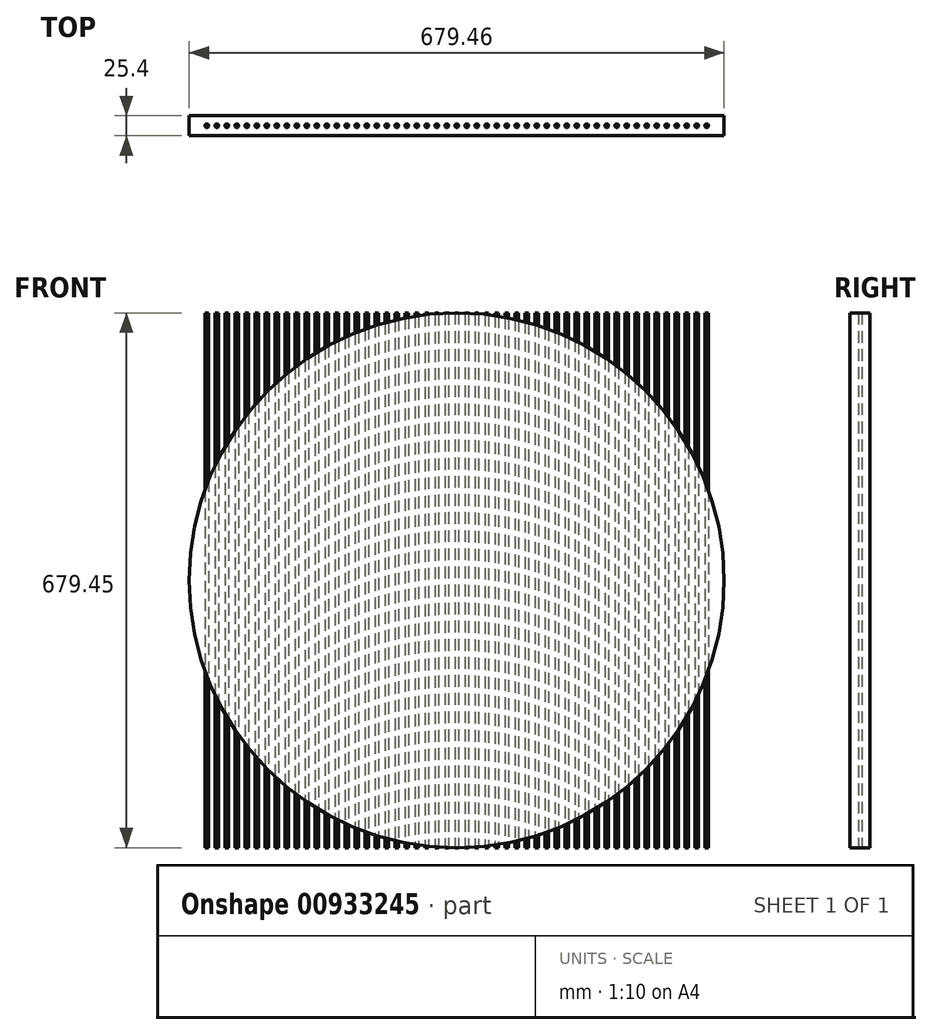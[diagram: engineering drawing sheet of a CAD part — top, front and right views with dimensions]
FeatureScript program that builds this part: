
annotation { "Feature Type Name" : "Feature", "Feature Type Description" : "" }
export const myFeature = defineFeature(function(context is Context, id is Id, definition is map)
    precondition{}
    {
        {
            var Q0;
            Q0=qCreatedBy(makeId("Top.planeOp"),FACE);
            var sketch = newSketch(context, id + "F0", { "sketchPlane" : qUnion([Q0])});
            skCircle(sketch, "E0", {"center": v(0, 0) * mm, "radius": 2.39 * mm});
            skCircle(sketch, "E1.1.0.0", {"center": v(12.7, 0) * mm, "radius": 2.39 * mm});
            skCircle(sketch, "E1.2.0.0", {"center": v(25.4, 0) * mm, "radius": 2.39 * mm});
            skCircle(sketch, "E1.3.0.0", {"center": v(38.1, 0) * mm, "radius": 2.39 * mm});
            skCircle(sketch, "E1.4.0.0", {"center": v(50.8, 0) * mm, "radius": 2.39 * mm});
            skCircle(sketch, "E1.5.0.0", {"center": v(63.5, 0) * mm, "radius": 2.39 * mm});
            skCircle(sketch, "E1.6.0.0", {"center": v(76.2, 0) * mm, "radius": 2.39 * mm});
            skCircle(sketch, "E1.7.0.0", {"center": v(88.9, 0) * mm, "radius": 2.39 * mm});
            skCircle(sketch, "E1.8.0.0", {"center": v(101.6, 0) * mm, "radius": 2.39 * mm});
            skCircle(sketch, "E1.9.0.0", {"center": v(114.3, 0) * mm, "radius": 2.39 * mm});
            skCircle(sketch, "E1.10.0.0", {"center": v(127, 0) * mm, "radius": 2.39 * mm});
            skCircle(sketch, "E1.11.0.0", {"center": v(139.7, 0) * mm, "radius": 2.39 * mm});
            skCircle(sketch, "E1.12.0.0", {"center": v(152.4, 0) * mm, "radius": 2.39 * mm});
            skCircle(sketch, "E1.13.0.0", {"center": v(165.1, 0) * mm, "radius": 2.39 * mm});
            skCircle(sketch, "E1.14.0.0", {"center": v(177.8, 0) * mm, "radius": 2.39 * mm});
            skCircle(sketch, "E1.15.0.0", {"center": v(190.5, 0) * mm, "radius": 2.39 * mm});
            skCircle(sketch, "E1.16.0.0", {"center": v(203.2, 0) * mm, "radius": 2.39 * mm});
            skCircle(sketch, "E1.17.0.0", {"center": v(215.9, 0) * mm, "radius": 2.39 * mm});
            skCircle(sketch, "E1.18.0.0", {"center": v(228.6, 0) * mm, "radius": 2.39 * mm});
            skCircle(sketch, "E1.19.0.0", {"center": v(241.3, 0) * mm, "radius": 2.39 * mm});
            skCircle(sketch, "E1.20.0.0", {"center": v(254, 0) * mm, "radius": 2.39 * mm});
            skCircle(sketch, "E1.21.0.0", {"center": v(266.7, 0) * mm, "radius": 2.39 * mm});
            skCircle(sketch, "E1.22.0.0", {"center": v(279.4, 0) * mm, "radius": 2.39 * mm});
            skCircle(sketch, "E1.23.0.0", {"center": v(292.1, 0) * mm, "radius": 2.39 * mm});
            skCircle(sketch, "E1.24.0.0", {"center": v(304.8, 0) * mm, "radius": 2.39 * mm});
            skCircle(sketch, "E1.25.0.0", {"center": v(317.5, 0) * mm, "radius": 2.39 * mm});
            skLineSegment(sketch, "E1.direction1", {"start": v(0, 0) * mm, "end": v(12.7, 0) * mm, "construction": true});
            skCircle(sketch, "E2.1.0.0", {"center": v(-12.7, 0) * mm, "radius": 2.39 * mm});
            skCircle(sketch, "E2.2.0.0", {"center": v(-25.4, 0) * mm, "radius": 2.39 * mm});
            skCircle(sketch, "E2.3.0.0", {"center": v(-38.1, 0) * mm, "radius": 2.39 * mm});
            skCircle(sketch, "E2.4.0.0", {"center": v(-50.8, 0) * mm, "radius": 2.39 * mm});
            skCircle(sketch, "E2.5.0.0", {"center": v(-63.5, 0) * mm, "radius": 2.39 * mm});
            skCircle(sketch, "E2.6.0.0", {"center": v(-76.2, 0) * mm, "radius": 2.39 * mm});
            skCircle(sketch, "E2.7.0.0", {"center": v(-88.9, 0) * mm, "radius": 2.39 * mm});
            skCircle(sketch, "E2.8.0.0", {"center": v(-101.6, 0) * mm, "radius": 2.39 * mm});
            skCircle(sketch, "E2.9.0.0", {"center": v(-114.3, 0) * mm, "radius": 2.39 * mm});
            skCircle(sketch, "E2.10.0.0", {"center": v(-127, 0) * mm, "radius": 2.39 * mm});
            skCircle(sketch, "E2.11.0.0", {"center": v(-139.7, 0) * mm, "radius": 2.39 * mm});
            skCircle(sketch, "E2.12.0.0", {"center": v(-152.4, 0) * mm, "radius": 2.39 * mm});
            skCircle(sketch, "E2.13.0.0", {"center": v(-165.1, 0) * mm, "radius": 2.39 * mm});
            skCircle(sketch, "E2.14.0.0", {"center": v(-177.8, 0) * mm, "radius": 2.39 * mm});
            skCircle(sketch, "E2.15.0.0", {"center": v(-190.5, 0) * mm, "radius": 2.39 * mm});
            skCircle(sketch, "E2.16.0.0", {"center": v(-203.2, 0) * mm, "radius": 2.39 * mm});
            skCircle(sketch, "E2.17.0.0", {"center": v(-215.9, 0) * mm, "radius": 2.39 * mm});
            skCircle(sketch, "E2.18.0.0", {"center": v(-228.6, 0) * mm, "radius": 2.39 * mm});
            skCircle(sketch, "E2.19.0.0", {"center": v(-241.3, 0) * mm, "radius": 2.39 * mm});
            skCircle(sketch, "E2.20.0.0", {"center": v(-254, 0) * mm, "radius": 2.39 * mm});
            skCircle(sketch, "E2.21.0.0", {"center": v(-266.7, 0) * mm, "radius": 2.39 * mm});
            skCircle(sketch, "E2.22.0.0", {"center": v(-279.4, 0) * mm, "radius": 2.39 * mm});
            skCircle(sketch, "E2.23.0.0", {"center": v(-292.1, 0) * mm, "radius": 2.39 * mm});
            skCircle(sketch, "E2.24.0.0", {"center": v(-304.8, 0) * mm, "radius": 2.39 * mm});
            skCircle(sketch, "E2.25.0.0", {"center": v(-317.5, 0) * mm, "radius": 2.39 * mm});
            skLineSegment(sketch, "E2.direction1", {"start": v(0, 0) * mm, "end": v(-12.7, 0) * mm, "construction": true});
            skSolve(sketch);
        }
        {
            var Q0;
            Q0 = qSketchRegion(id + "F0", true);
            extrude(context, id + "F1", {"entities" : qUnion([Q0]), "depth" : 679.45 * mm, "offsetDistance" : 25.4 * mm});
        }
        {
            var Q0;
            Q0=qCreatedBy(makeId("Front.planeOp"),FACE);
            var sketch = newSketch(context, id + "F2", { "sketchPlane" : qUnion([Q0])});
            skCircle(sketch, "E3", {"center": v(0, 339.73) * mm, "radius": 339.73 * mm});
            skSolve(sketch);
        }
        {
            var Q0;
            Q0=makeQuery(id+"F2.imprint","IMPRINT",FACE,{"disambiguationData":[TD([[makeQuery(id+"F2.imprint","IMPRINT",EDGE,{"derivedFrom":sQuery(id+"F2.wireOp",EDGE,"E3")}),1.0]])]});
            extrude(context, id + "F3", {"entities" : qUnion([Q0]), "endBound" : BoundingType.SYMMETRIC, "oppositeDirection" : true, "depth" : 25.4 * mm, "offsetDistance" : 25.4 * mm});
        }
    });
